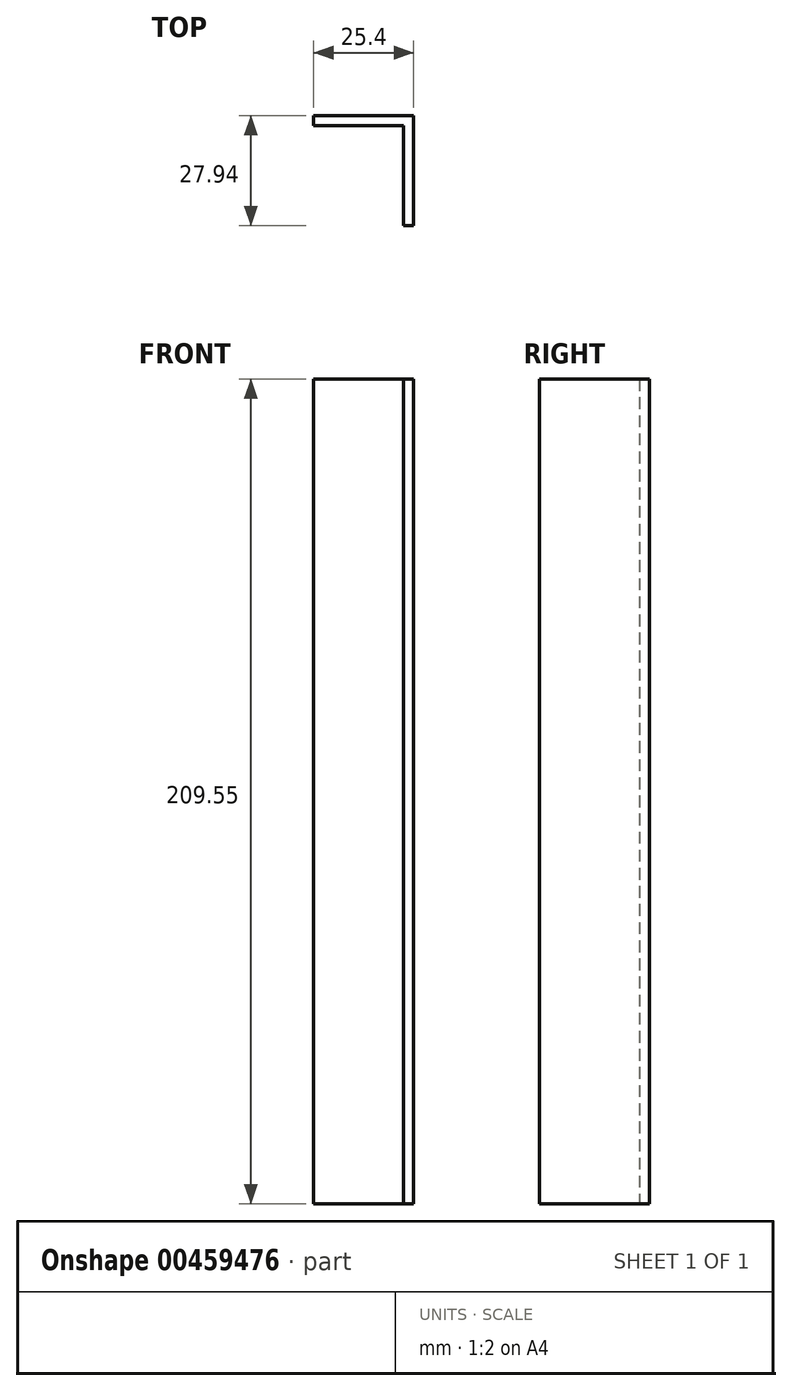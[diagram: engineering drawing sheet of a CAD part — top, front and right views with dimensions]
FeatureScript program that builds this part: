
annotation { "Feature Type Name" : "Feature", "Feature Type Description" : "" }
export const myFeature = defineFeature(function(context is Context, id is Id, definition is map)
    precondition{}
    {
        {
            var Q0;
            Q0=qCreatedBy(makeId("Right.planeOp"),FACE);
            var sketch = newSketch(context, id + "F0", { "sketchPlane" : qUnion([Q0])});
            skLineSegment(sketch, "E0", {"start": v(31.7, 65.33) * mm, "end": v(3.76, 65.33) * mm});
            skLineSegment(sketch, "E1", {"start": v(3.76, 65.33) * mm, "end": v(3.76, -144.22) * mm});
            skLineSegment(sketch, "E2", {"start": v(3.76, -144.22) * mm, "end": v(31.7, -144.22) * mm});
            skLineSegment(sketch, "E3", {"start": v(31.7, -144.22) * mm, "end": v(31.7, 65.33) * mm});
            skSolve(sketch);
        }
        {
            var Q0;
            Q0=makeQuery(id+"F0.imprint","IMPRINT",FACE,{"disambiguationData":[TD([[makeQuery(id+"F0.imprint","IMPRINT",EDGE,{"derivedFrom":sQuery(id+"F0.wireOp",EDGE,"E0")}),1.0]])]});
            extrude(context, id + "F1", {"entities" : qUnion([Q0]), "oppositeDirection" : true, "depth" : 2.54 * mm});
        }
        {
            var Q0;
            Q0=makeQuery(id+"F1.opExtrude","CAP_FACE",FACE,{"disambiguationData":[OSD([sQuery(id+"F0.wireOp",EDGE,"E0"),sQuery(id+"F0.wireOp",EDGE,"E1"),sQuery(id+"F0.wireOp",EDGE,"E2"),sQuery(id+"F0.wireOp",EDGE,"E3")])],"isStart":false});
            var sketch = newSketch(context, id + "F2", { "sketchPlane" : qUnion([Q0])});
            skLineSegment(sketch, "E4", {"start": v(-31.7, 65.33) * mm, "end": v(-29.16, 65.33) * mm});
            skLineSegment(sketch, "E5", {"start": v(-29.16, 65.33) * mm, "end": v(-29.16, -144.22) * mm});
            skLineSegment(sketch, "E6", {"start": v(-29.16, -144.22) * mm, "end": v(-31.7, -144.22) * mm});
            skLineSegment(sketch, "E7", {"start": v(-31.7, -144.22) * mm, "end": v(-31.7, 65.33) * mm});
            skSolve(sketch);
        }
        {
            var Q0;
            Q0=makeQuery(id+"F2.imprint","IMPRINT",FACE,{"disambiguationData":[TD([[makeQuery(id+"F2.imprint","IMPRINT",EDGE,{"derivedFrom":sQuery(id+"F2.wireOp",EDGE,"E4")}),-1.0]])]});
            extrude(context, id + "F3", {"entities" : qUnion([Q0]), "operationType" : NewBodyOperationType.ADD, "depth" : 22.86 * mm});
        }
    });
